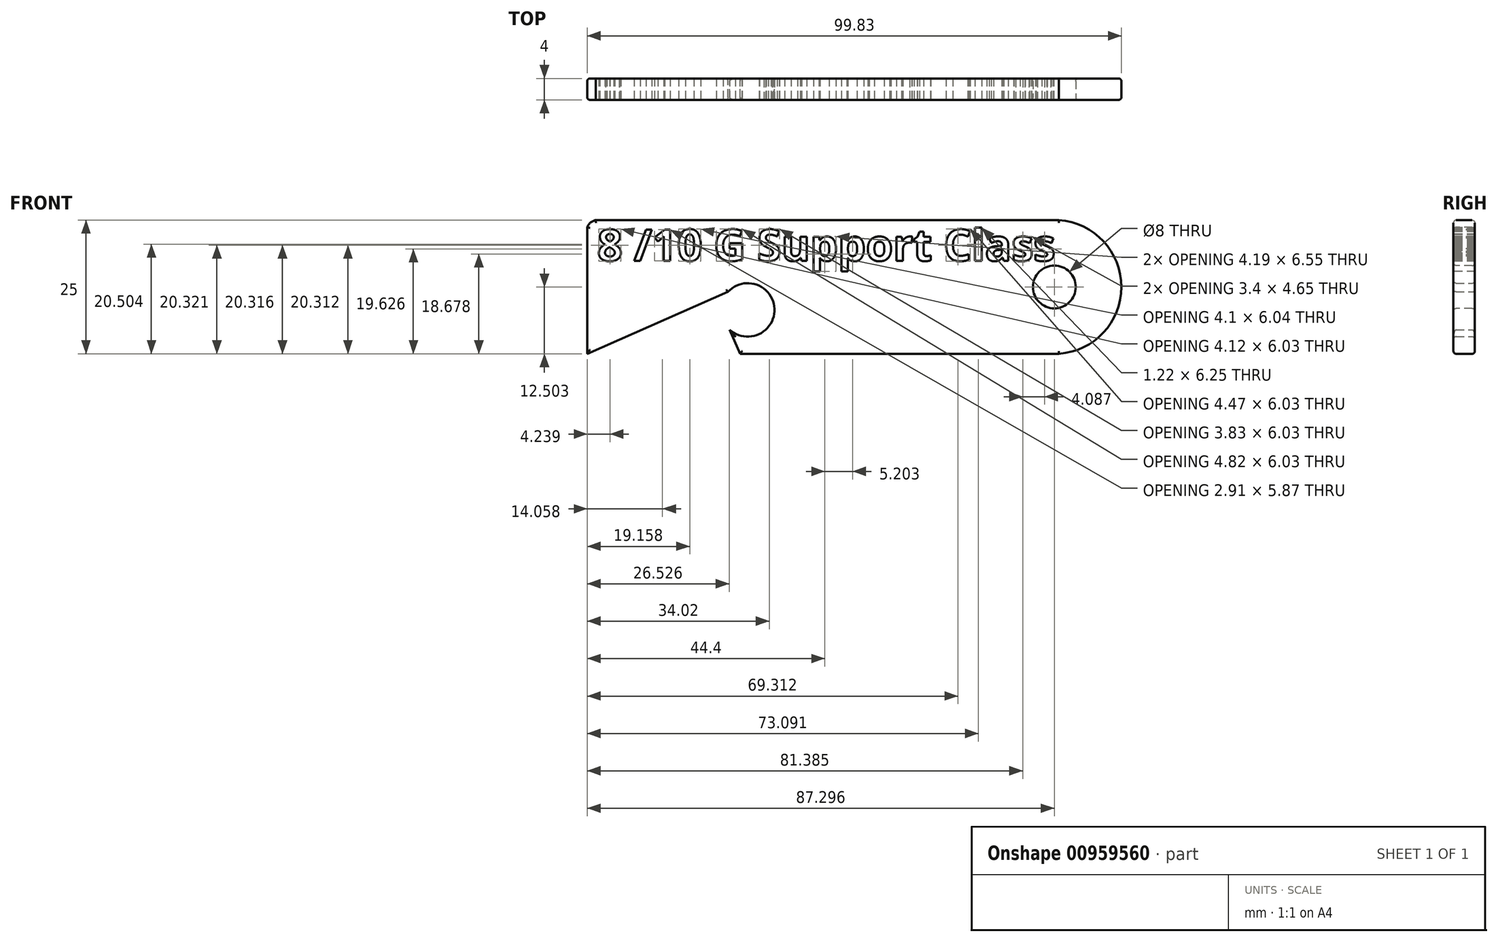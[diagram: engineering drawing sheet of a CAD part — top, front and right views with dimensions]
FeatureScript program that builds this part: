
annotation { "Feature Type Name" : "Feature", "Feature Type Description" : "" }
export const myFeature = defineFeature(function(context is Context, id is Id, definition is map)
    precondition{}
    {
        {
            var Q0;
            Q0=qCreatedBy(makeId("Front.planeOp"),FACE);
            var sketch = newSketch(context, id + "F0", { "sketchPlane" : qUnion([Q0])});
            skLineSegment(sketch, "E0.bottom", {"start": v(-6.84, -8.2) * mm, "end": v(93.16, -8.2) * mm});
            skLineSegment(sketch, "E0.top", {"start": v(-6.84, 16.8) * mm, "end": v(93.16, 16.8) * mm});
            skLineSegment(sketch, "E0.left", {"start": v(-6.84, -8.2) * mm, "end": v(-6.84, 16.8) * mm});
            skLineSegment(sketch, "E0.right", {"start": v(93.16, -8.2) * mm, "end": v(93.16, 16.8) * mm});
            skArc(sketch, "E1", {"start": v(81.33, -8.2) * mm, "mid": v(92.96, 5.17) * mm, "end": v(79.58, 16.8) * mm});
            skCircle(sketch, "E2", {"center": v(23.16, 0) * mm, "radius": 5 * mm});
            skLineSegment(sketch, "E3", {"start": v(-6.84, -8.2) * mm, "end": v(23.16, 5) * mm});
            skLineSegment(sketch, "E4", {"start": v(18.16, 0) * mm, "end": v(21.77, -8.2) * mm});
            skPoint(sketch, "E4.endSnap0", {"position": v(43.16, -8.2) * mm});
            skSolve(sketch);
        }
        {
            var Q0;
            {var subQ4=sQuery(id+"F0.wireOp",EDGE,"E0.left");Q0=makeQuery(id+"F0.imprint","IMPRINT",FACE,{"disambiguationData":[TD([[makeQuery(id+"F0.imprint","IMPRINT",EDGE,{"derivedFrom":subQ4}),-1.0]])]});}
            extrude(context, id + "F1", {"entities" : qUnion([Q0]), "depth" : 4 * mm, "offsetDistance" : 25 * mm});
        }
        {
            var Q0;
            Q0=makeQuery(id+"F1.opExtrude","CAP_FACE",FACE,{"disambiguationData":[OSD([sQuery(id+"F0.wireOp",EDGE,"E0.bottom"),sQuery(id+"F0.wireOp",EDGE,"E0.top"),sQuery(id+"F0.wireOp",EDGE,"E0.left"),sQuery(id+"F0.wireOp",EDGE,"E1"),sQuery(id+"F0.wireOp",EDGE,"E2"),sQuery(id+"F0.wireOp",EDGE,"E3"),sQuery(id+"F0.wireOp",EDGE,"E4")])],"isStart":false});
            var sketch = newSketch(context, id + "F2", { "sketchPlane" : qUnion([Q0])});
            skCircle(sketch, "E5", {"center": v(80.46, 4.3) * mm, "radius": 4 * mm});
            skSolve(sketch);
        }
        {
            var Q0;
            Q0=makeQuery(id+"F2.imprint","IMPRINT",FACE,{"disambiguationData":[TD([[makeQuery(id+"F2.imprint","IMPRINT",EDGE,{"derivedFrom":sQuery(id+"F2.wireOp",EDGE,"E5")}),1.0]])]});
            extrude(context, id + "F3", {"entities" : qUnion([Q0]), "operationType" : NewBodyOperationType.REMOVE, "endBound" : BoundingType.THROUGH_ALL, "oppositeDirection" : true, "depth" : 25 * mm, "offsetDistance" : 25 * mm});
        }
        {
            var Q0;
            Q0=makeQuery(id+"F1.opExtrude","CAP_FACE",FACE,{"disambiguationData":[OSD([sQuery(id+"F0.wireOp",EDGE,"E0.bottom"),sQuery(id+"F0.wireOp",EDGE,"E0.top"),sQuery(id+"F0.wireOp",EDGE,"E0.left"),sQuery(id+"F0.wireOp",EDGE,"E1"),sQuery(id+"F0.wireOp",EDGE,"E2"),sQuery(id+"F0.wireOp",EDGE,"E3"),sQuery(id+"F0.wireOp",EDGE,"E4")])],"isStart":false});
            var sketch = newSketch(context, id + "F4", { "sketchPlane" : qUnion([Q0])});
            skArc(sketch, "E6", {"start": v(-4.63, 16.8) * mm, "mid": v(-6.46, 16.11) * mm, "end": v(-6.84, 14.2) * mm});
            skSolve(sketch);
        }
        {
            var Q0;
            {var subQ0=sQuery(id+"F4.wireOp",EDGE,"E6");var subQ1=makeQuery(id+"F1.opExtrude","CAP_EDGE",EDGE,{"disambiguationData":[OSD([sQuery(id+"F0.wireOp",EDGE,"E0.top")])],"isStart":false});var subQ2=makeQuery(id+"F4.imprint","INTERSECT",VERTEX,{"disambiguationData":[OD(1.0)],"derivedFrom":[subQ1,subQ0]});Q0=makeQuery(id+"F4.imprint","IMPRINT",FACE,{"disambiguationData":[TD([[makeQuery(id+"F4.imprint","IMPRINT",EDGE,{"disambiguationData":[TD([[subQ2,-1.0]])],"derivedFrom":subQ0}),-1.0]])]});}
            extrude(context, id + "F5", {"entities" : qUnion([Q0]), "operationType" : NewBodyOperationType.REMOVE, "endBound" : BoundingType.THROUGH_ALL, "oppositeDirection" : true, "depth" : 25 * mm, "offsetDistance" : 25 * mm});
        }
        {
            var Q0;
            Q0=makeQuery(id+"F1.opExtrude","CAP_FACE",FACE,{"disambiguationData":[OSD([sQuery(id+"F0.wireOp",EDGE,"E0.bottom"),sQuery(id+"F0.wireOp",EDGE,"E0.top"),sQuery(id+"F0.wireOp",EDGE,"E0.left"),sQuery(id+"F0.wireOp",EDGE,"E1"),sQuery(id+"F0.wireOp",EDGE,"E2"),sQuery(id+"F0.wireOp",EDGE,"E3"),sQuery(id+"F0.wireOp",EDGE,"E4")])],"isStart":false});
            fillet(context, id + "F6", {"entities" : qUnion([Q0]), "radius" : .5 * mm, "tangentPropagation" : true, "allowEdgeOverflow" : false});
        }
        {
            var Q0;
            Q0=makeQuery(id+"F1.opExtrude","CAP_FACE",FACE,{"disambiguationData":[OSD([sQuery(id+"F0.wireOp",EDGE,"E0.bottom"),sQuery(id+"F0.wireOp",EDGE,"E0.top"),sQuery(id+"F0.wireOp",EDGE,"E0.left"),sQuery(id+"F0.wireOp",EDGE,"E1"),sQuery(id+"F0.wireOp",EDGE,"E2"),sQuery(id+"F0.wireOp",EDGE,"E3"),sQuery(id+"F0.wireOp",EDGE,"E4")])],"isStart":true});
            fillet(context, id + "F7", {"entities" : qUnion([Q0]), "radius" : .5 * mm, "tangentPropagation" : true, "allowEdgeOverflow" : false});
        }
        {
            var Q0;
            Q0=makeQuery(id+"F1.opExtrude","CAP_FACE",FACE,{"disambiguationData":[OSD([sQuery(id+"F0.wireOp",EDGE,"E0.bottom"),sQuery(id+"F0.wireOp",EDGE,"E0.top"),sQuery(id+"F0.wireOp",EDGE,"E0.left"),sQuery(id+"F0.wireOp",EDGE,"E1"),sQuery(id+"F0.wireOp",EDGE,"E2"),sQuery(id+"F0.wireOp",EDGE,"E3"),sQuery(id+"F0.wireOp",EDGE,"E4")])],"isStart":false});
            var sketch = newSketch(context, id + "F8", { "sketchPlane" : qUnion([Q0])});
            skText(sketch, "E7", { "text": "8 /10 G Support Class", "fontName": "OpenSans-Bold.ttf"});
            const initialGuessF8  = {"E7": [-0.00495, 0.00917, 1, 0, 0.00592]};
            skSetInitialGuess(sketch, initialGuessF8);
            skSolve(sketch);
        }
        {
            var Q0;
            Q0 = qSketchRegion(id + "F8", true);
            extrude(context, id + "F9", {"entities" : qUnion([Q0]), "operationType" : NewBodyOperationType.REMOVE, "endBound" : BoundingType.THROUGH_ALL, "oppositeDirection" : true, "depth" : .8 * mm, "offsetDistance" : 25 * mm});
        }
    });
